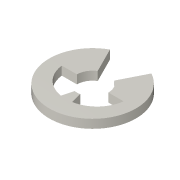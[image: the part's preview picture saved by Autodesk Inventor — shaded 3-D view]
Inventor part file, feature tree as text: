
AUTODESK INVENTOR PART (.ipt)
format: ipt  version: 2016 SP1 (Build 200210100, 210)  size: 103,936 bytes
history: native  units: mm
features: extrude x2, sketch x2
ambient origin geometry x8: Origin, YZ Plane, XZ Plane, XY Plane, X Axis, Y Axis, Z Axis, Center Point
bodies: Volumenkörper1 (feature_tree)
feature tree (4):
  extrude  "Extrusion1"  Depth=0.4mm TaperAngle=0.0deg
  extrude  "Extrusion2"  Depth=1.4mm
  sketch  "Skizze1"  dims[d0=4.0mm d1=0.4mm d2=0.0mm]
  sketch  "Skizze2"  dims[d3=1.45mm d4=1.4mm d5=1.4mm d6=75.0deg d7=75.0deg d8=0.7mm d9=0.7mm d10=0.5mm d11=0.5mm d12=0.4mm d13=0.0mm]
